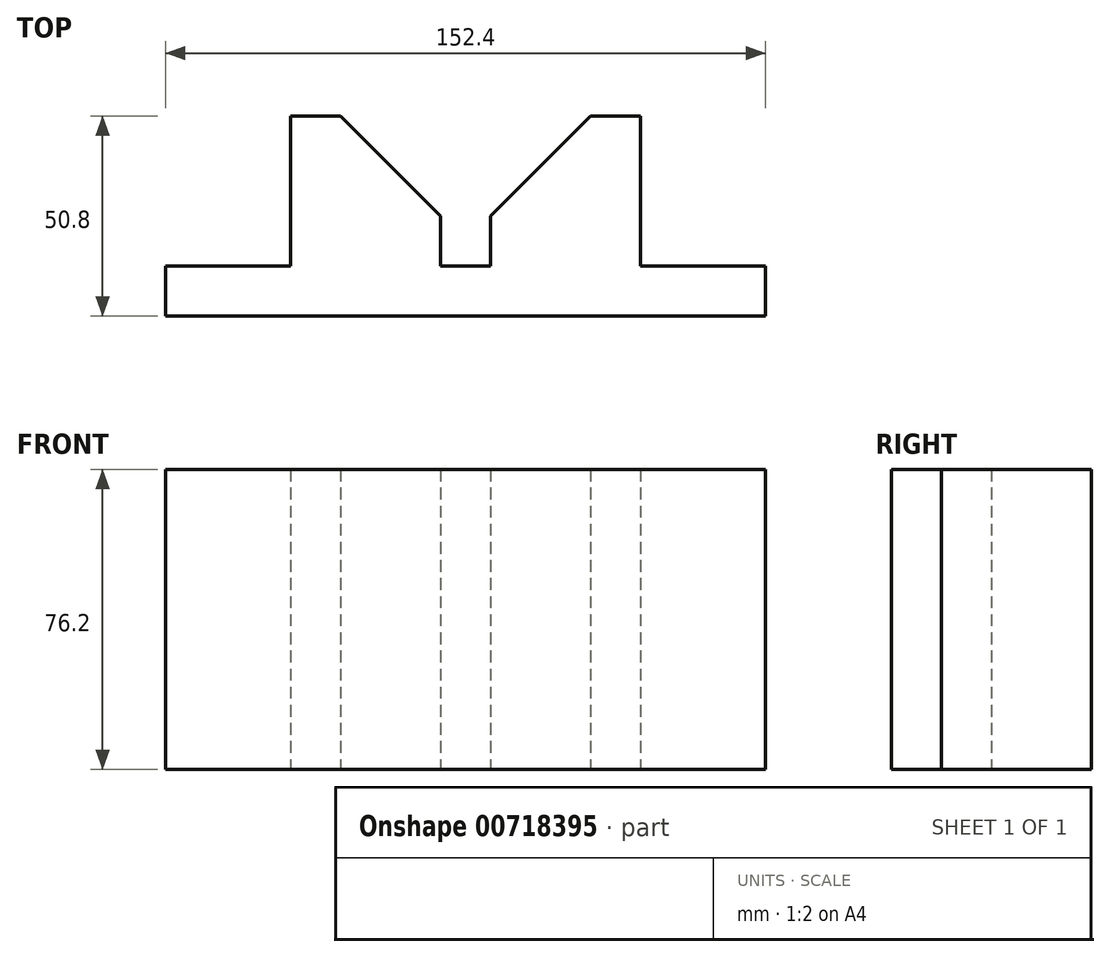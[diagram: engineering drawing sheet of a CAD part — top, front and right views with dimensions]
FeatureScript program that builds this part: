
annotation { "Feature Type Name" : "Feature", "Feature Type Description" : "" }
export const myFeature = defineFeature(function(context is Context, id is Id, definition is map)
    precondition{}
    {
        {
            var Q0;
            Q0=qCreatedBy(makeId("Top.planeOp"),FACE);
            var sketch = newSketch(context, id + "F0", { "sketchPlane" : qUnion([Q0])});
            skLineSegment(sketch, "E0", {"start": v(-71.54, 10.88) * mm, "end": v(-71.54, -1.82) * mm});
            skLineSegment(sketch, "E1", {"start": v(-71.54, -1.82) * mm, "end": v(80.86, -1.82) * mm});
            skLineSegment(sketch, "E2", {"start": v(80.86, -1.82) * mm, "end": v(80.86, 10.88) * mm});
            skLineSegment(sketch, "E3", {"start": v(80.86, 10.88) * mm, "end": v(49.11, 10.88) * mm});
            skLineSegment(sketch, "E4", {"start": v(49.11, 10.88) * mm, "end": v(49.11, 48.98) * mm});
            skLineSegment(sketch, "E5", {"start": v(49.11, 48.98) * mm, "end": v(36.41, 48.98) * mm});
            skLineSegment(sketch, "E6", {"start": v(-71.54, 10.88) * mm, "end": v(-39.79, 10.88) * mm});
            skLineSegment(sketch, "E7", {"start": v(-39.79, 10.88) * mm, "end": v(-39.79, 48.98) * mm});
            skLineSegment(sketch, "E8", {"start": v(-39.79, 48.98) * mm, "end": v(-27.09, 48.98) * mm});
            skLineSegment(sketch, "E9", {"start": v(-1.69, 10.88) * mm, "end": v(-1.69, 23.58) * mm});
            skLineSegment(sketch, "E10", {"start": v(-1.69, 10.88) * mm, "end": v(11.01, 10.88) * mm});
            skLineSegment(sketch, "E11", {"start": v(11.01, 10.88) * mm, "end": v(11.01, 23.58) * mm});
            skLineSegment(sketch, "E12", {"start": v(-27.09, 48.98) * mm, "end": v(-1.69, 23.58) * mm});
            skLineSegment(sketch, "E13", {"start": v(11.01, 23.58) * mm, "end": v(36.41, 48.98) * mm});
            skSolve(sketch);
        }
        {
            var Q0;
            Q0=makeQuery(id+"F0.imprint","IMPRINT",FACE,{"disambiguationData":[TD([[makeQuery(id+"F0.imprint","IMPRINT",EDGE,{"derivedFrom":sQuery(id+"F0.wireOp",EDGE,"E0")}),1.0]])]});
            extrude(context, id + "F1", {"entities" : qUnion([Q0]), "depth" : 76.2 * mm, "offsetDistance" : 25.4 * mm});
        }
    });
